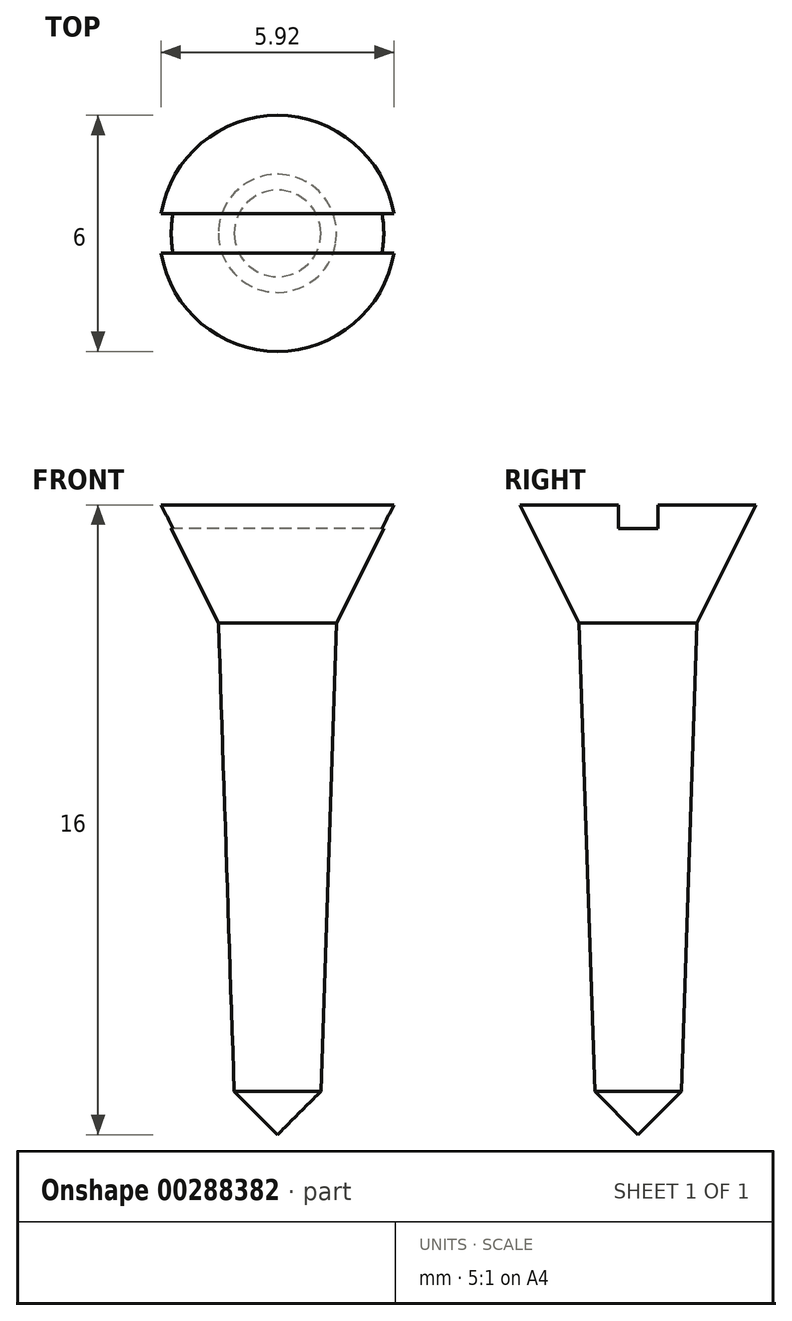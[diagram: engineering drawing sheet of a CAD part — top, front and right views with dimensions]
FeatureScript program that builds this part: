
annotation { "Feature Type Name" : "Feature", "Feature Type Description" : "" }
export const myFeature = defineFeature(function(context is Context, id is Id, definition is map)
    precondition{}
    {
        {
            var Q0;
            Q0=qCreatedBy(makeId("Front.planeOp"),FACE);
            var sketch = newSketch(context, id + "F0", { "sketchPlane" : qUnion([Q0])});
            skLineSegment(sketch, "E0", {"start": v(0, 0) * mm, "end": v(0, 16) * mm});
            skLineSegment(sketch, "E1", {"start": v(0, 16) * mm, "end": v(3, 16) * mm});
            skLineSegment(sketch, "E2", {"start": v(3, 16) * mm, "end": v(1.5, 13) * mm});
            skLineSegment(sketch, "E3", {"start": v(1.5, 13) * mm, "end": v(1.1, 1.1) * mm});
            skLineSegment(sketch, "E4", {"start": v(1.1, 1.1) * mm, "end": v(0, 0) * mm});
            skSolve(sketch);
        }
        {
            var Q0;
            Q0=makeQuery(id+"F0.imprint","IMPRINT",FACE,{"disambiguationData":[TD([[makeQuery(id+"F0.imprint","IMPRINT",EDGE,{"derivedFrom":sQuery(id+"F0.wireOp",EDGE,"E0")}),-1.0]])]});
            var Q1;
            Q1=sQuery(id+"F0.wireOp",EDGE,"E0");
            revolve(context, id + "F1", {"entities" : qUnion([Q0]), "axis" : qUnion([Q1]), "revolveType" : RevolveType.FULL});
        }
        {
            var Q0;
            Q0=qCreatedBy(makeId("Top.planeOp"),FACE);
            cPlane(context, id + "F2", {"entities" : qUnion([Q0]), "cplaneType" : CPlaneType.OFFSET, "offset" : 16 * mm, "width" : 150 * mm, "height" : 150 * mm});
        }
        {
            var Q0;
            Q0=qCreatedBy(id+"F2.planeOp",FACE);
            var sketch = newSketch(context, id + "F3", { "sketchPlane" : qUnion([Q0])});
            skLineSegment(sketch, "E5.bottom", {"start": v(4, 0.5) * mm, "end": v(-4, 0.5) * mm});
            skLineSegment(sketch, "E5.top", {"start": v(4, -0.5) * mm, "end": v(-4, -0.5) * mm});
            skLineSegment(sketch, "E5.left", {"start": v(4, 0.5) * mm, "end": v(4, -0.5) * mm});
            skLineSegment(sketch, "E5.right", {"start": v(-4, 0.5) * mm, "end": v(-4, -0.5) * mm});
            skPoint(sketch, "E5.middle", {"position": v(0, 0) * mm});
            skSolve(sketch);
        }
        {
            var Q0;
            Q0 = qSketchRegion(id + "F3", true);
            extrude(context, id + "F4", {"entities" : qUnion([Q0]), "operationType" : NewBodyOperationType.REMOVE, "oppositeDirection" : true, "depth" : .6 * mm});
        }
    });
